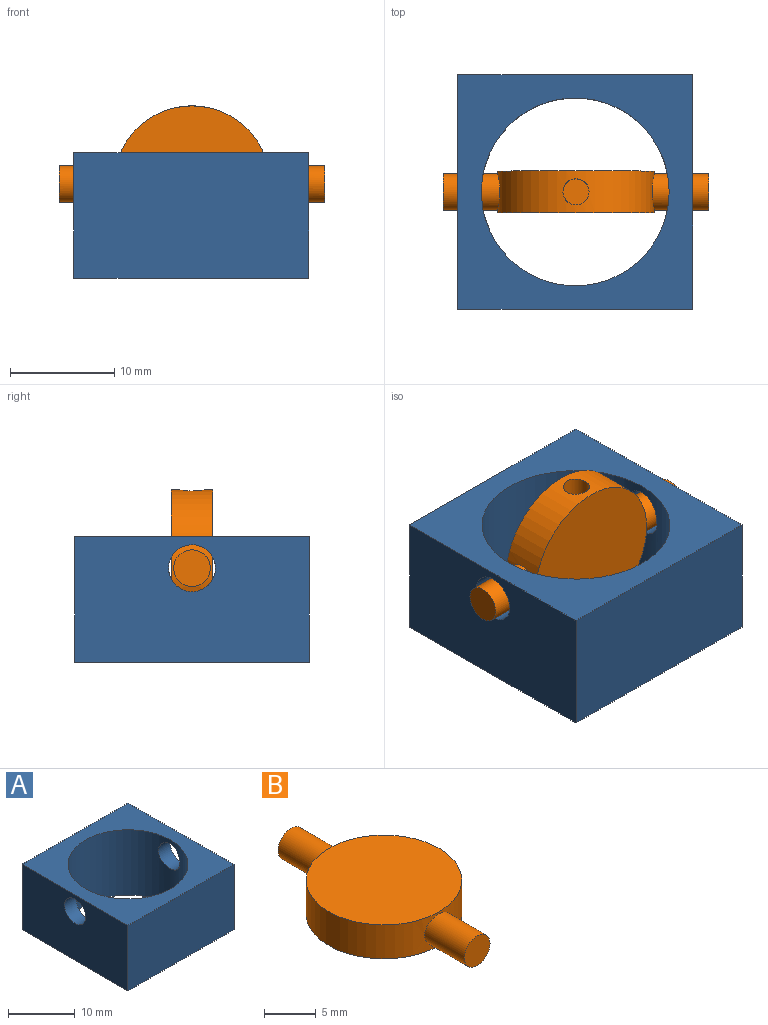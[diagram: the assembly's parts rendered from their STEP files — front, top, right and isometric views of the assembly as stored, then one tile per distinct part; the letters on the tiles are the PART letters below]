
ASSEMBLY  parts=2 mates=1
PART A: 9 faces, bbox 22.5x22.5x12 mm
  f0: plane 22.5x12mm, normal (1,0,0), area 254.1mm2, adj f1,f3,f5,f6,f7
  f1: plane 22.5x12mm, normal (0,1,0), area 270mm2, adj f0,f2,f5,f6
  f2: plane 22.5x12mm, normal (-1,0,0), area 254.1mm2, adj f1,f3,f5,f6,f8
  f3: plane 22.5x12mm, normal (0,-1,0), area 270mm2, adj f0,f2,f5,f6
  f4: cylinder r=9mm len=18mm, axis (0,0,-1), area 646.5mm2, adj f5,f6,f7,f8
  f5: plane 22.5x22.5mm, normal (0,0,1), area 251.8mm2, adj f0,f1,f2,f3,f4
  f6: plane 22.5x22.5mm, normal (0,0,-1), area 251.8mm2, adj f0,f1,f2,f3,f4
  f7: cylinder r=2.25mm len=4.5mm, axis (1,0,0), area 33.8mm2, adj f0,f4
  f8: cylinder r=2.25mm len=4.5mm, axis (1,0,0), area 33.8mm2, adj f2,f4
PART B: 9 faces, bbox 15x25.4x4 mm
  f0: cylinder r=7.5mm len=15mm, axis (0,0,-1), area 164.1mm2, adj f1,f2,f4,f5,f8
  f1: plane 15x15mm, normal (0,0,1), area 176.7mm2, adj f0
  f2: plane 15x15mm, normal (0,0,-1), area 176.7mm2, adj f0
  f3: plane 3.5x3.5mm, normal (0,1,0), area 9.6mm2, adj f4
  f4: cylinder r=1.75mm len=5.41mm, axis (0,1,0), area 58.3mm2, adj f0,f3
  f5: cylinder r=1.75mm len=5.41mm, axis (0,1,0), area 58.3mm2, adj f0,f6
  f6: plane 3.5x3.5mm, normal (0,-1,0), area 9.6mm2, adj f5
  f7: plane 2.5x2.5mm, normal (1,0,0), area 4.9mm2, adj f8
  f8: cylinder r=1.25mm len=12.6mm, axis (-1,0,0), area 98.5mm2, adj f0,f7
PLACE A t=(-5.03,3.33,0.47)mm
PLACE B rot(axis=(0.58,-0.58,0.58),120deg) t=(-4.96,3.33,9.47)mm
MATE cylindrical B.f4 <-> A.f7  axis (1,0,0) through (7.74,3.33,9.47)mm
